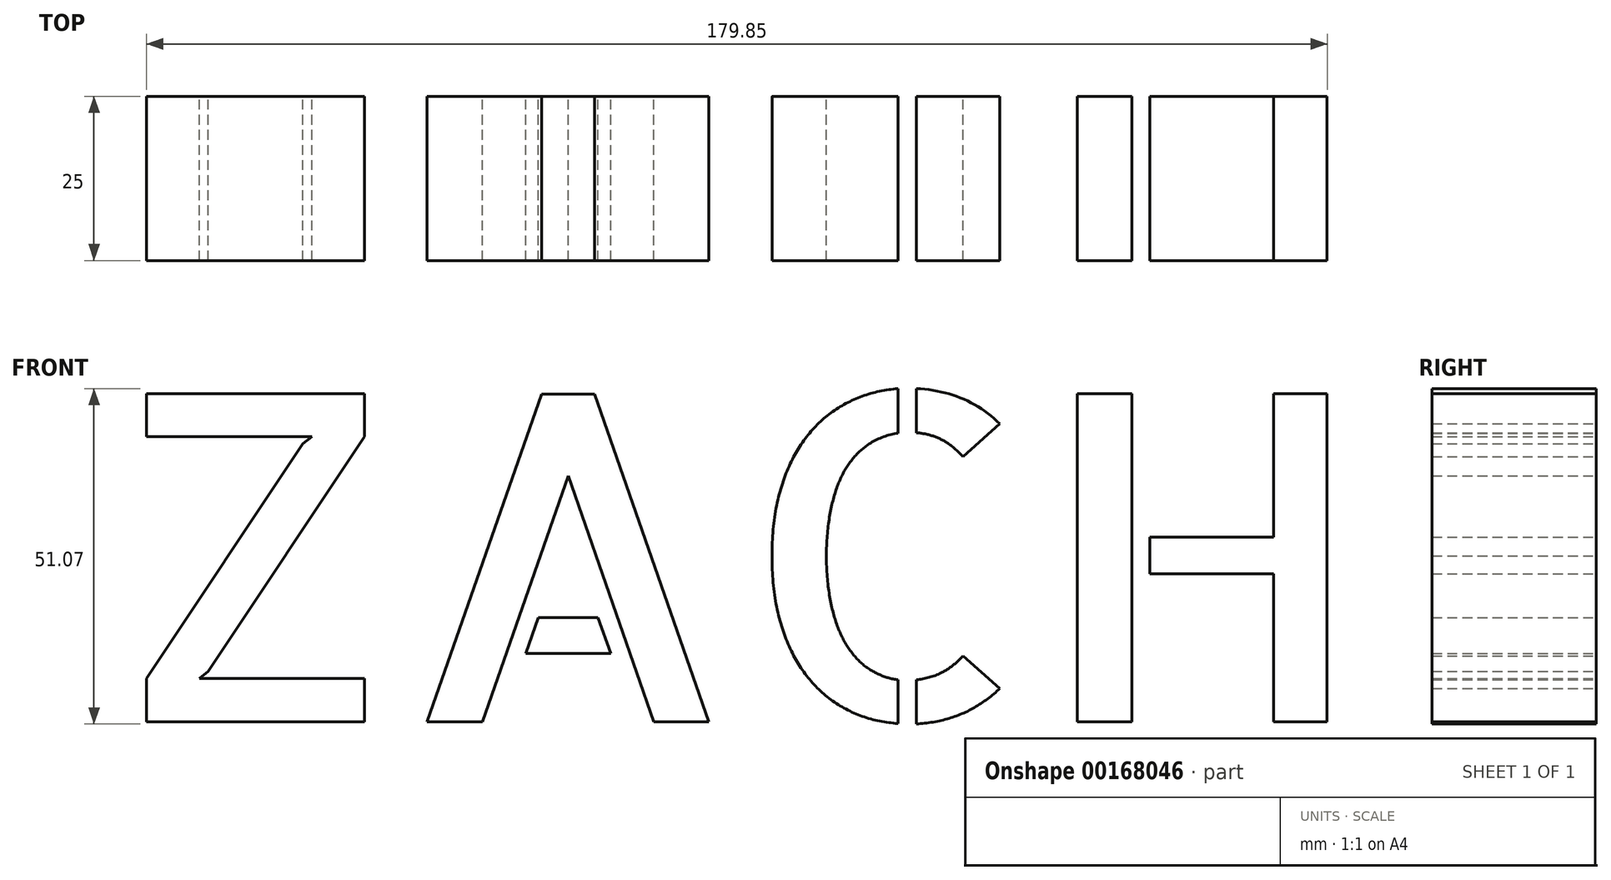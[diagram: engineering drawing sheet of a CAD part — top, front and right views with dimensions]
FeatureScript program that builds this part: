
annotation { "Feature Type Name" : "Feature", "Feature Type Description" : "" }
export const myFeature = defineFeature(function(context is Context, id is Id, definition is map)
    precondition{}
    {
        {
            var Q0;
            Q0=qCreatedBy(makeId("Front.planeOp"),FACE);
            var sketch = newSketch(context, id + "F0", { "sketchPlane" : qUnion([Q0])});
            skText(sketch, "E0", { "text": "ZACH", "fontName": "AllertaStencil-Regular.ttf"});
            const initialGuessF0  = {"E0": [-0.0949, 0, 1, 0, 0.05]};
            skSetInitialGuess(sketch, initialGuessF0);
            skSolve(sketch);
        }
        {
            var Q0;
            Q0=qSketchRegion(id+"F0",true);
            extrude(context, id + "F1", {"entities" : qUnion([Q0]), "depth" : 25 * mm});
        }
    });
